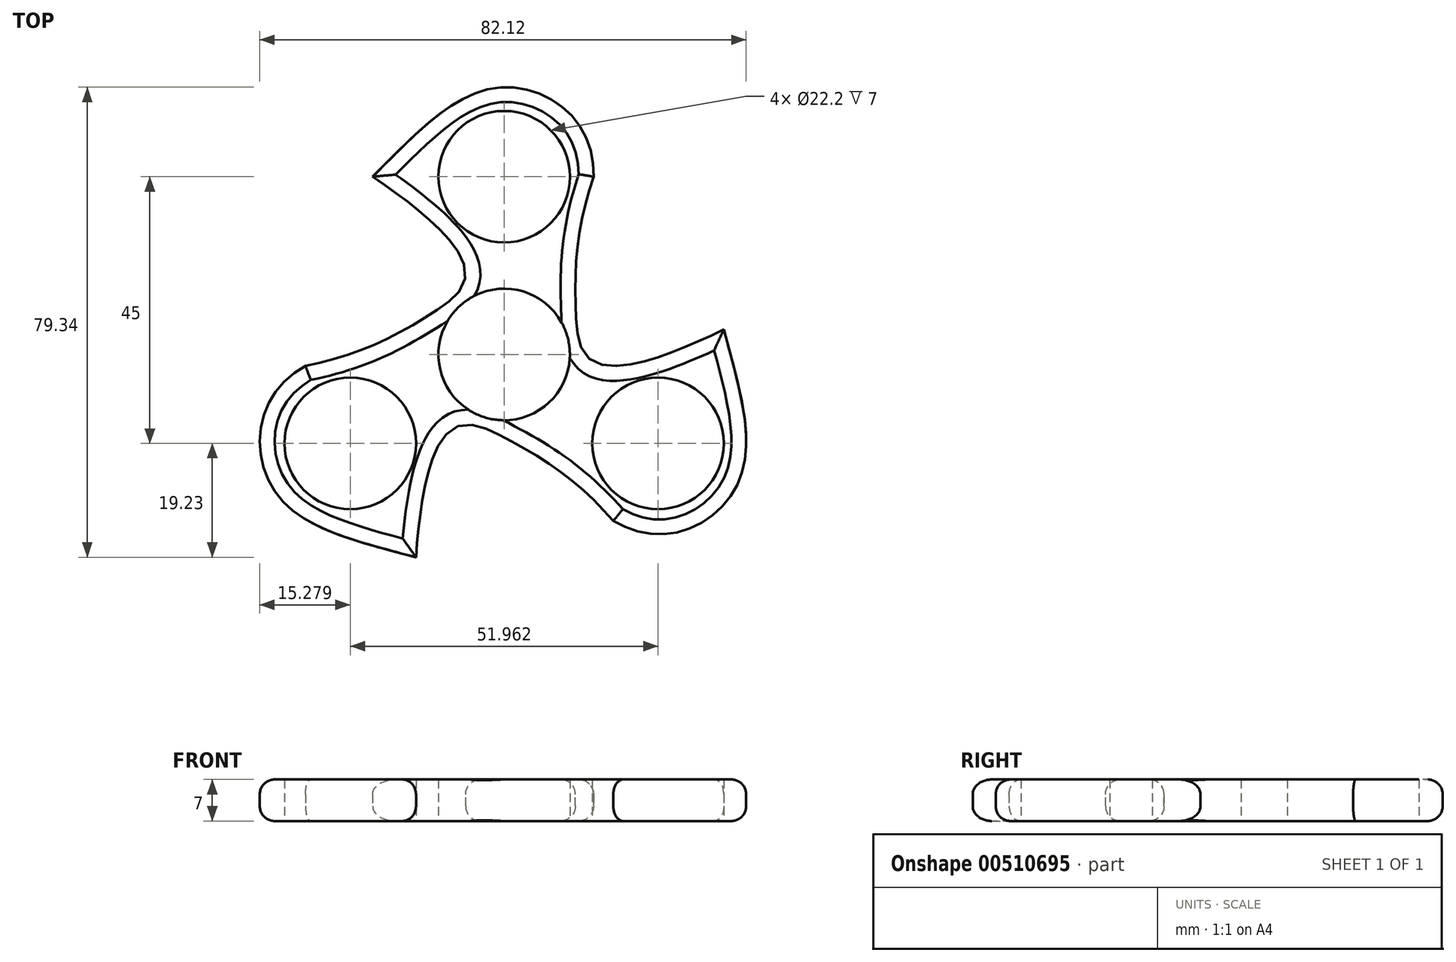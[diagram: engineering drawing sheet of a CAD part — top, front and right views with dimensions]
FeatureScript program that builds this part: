
annotation { "Feature Type Name" : "Feature", "Feature Type Description" : "" }
export const myFeature = defineFeature(function(context is Context, id is Id, definition is map)
    precondition{}
    {
        {
            var Q0;
            Q0=qCreatedBy(makeId("Top.planeOp"),FACE);
            var sketch = newSketch(context, id + "F0", { "sketchPlane" : qUnion([Q0])});
            skCircle(sketch, "E0", {"center": v(0, 0) * mm, "radius": 11.1 * mm});
            skCircle(sketch, "E1", {"center": v(0, 30) * mm, "radius": 11.1 * mm});
            skLineSegment(sketch, "E2", {"start": v(0, 0) * mm, "end": v(0, 30) * mm, "construction": true});
            skLineSegment(sketch, "E3", {"start": v(0, 30) * mm, "end": v(-22.2, 30) * mm, "construction": true});
            skLineSegment(sketch, "E4", {"start": v(0, 30) * mm, "end": v(15.1, 30) * mm, "construction": true});
            skLineSegment(sketch, "E5", {"start": v(0, 30) * mm, "end": v(0, 45.1) * mm, "construction": true});
            skLineSegment(sketch, "E6.1.0", {"start": v(-25.98, -15) * mm, "end": v(-33.53, -1.92) * mm, "construction": true});
            skLineSegment(sketch, "E6.1.1", {"start": v(-25.98, -15) * mm, "end": v(-39.06, -22.55) * mm, "construction": true});
            skLineSegment(sketch, "E6.1.2", {"start": v(-25.98, -15) * mm, "end": v(-14.88, -34.23) * mm, "construction": true});
            skCircle(sketch, "E6.1.3", {"center": v(-25.98, -15) * mm, "radius": 11.1 * mm});
            skLineSegment(sketch, "E6.1.4", {"start": v(0, 0) * mm, "end": v(-25.98, -15) * mm, "construction": true});
            skLineSegment(sketch, "E6.2.0", {"start": v(25.98, -15) * mm, "end": v(18.43, -28.08) * mm, "construction": true});
            skLineSegment(sketch, "E6.2.1", {"start": v(25.98, -15) * mm, "end": v(39.06, -22.55) * mm, "construction": true});
            skLineSegment(sketch, "E6.2.2", {"start": v(25.98, -15) * mm, "end": v(37.08, 4.23) * mm, "construction": true});
            skCircle(sketch, "E6.2.3", {"center": v(25.98, -15) * mm, "radius": 11.1 * mm});
            skLineSegment(sketch, "E6.2.4", {"start": v(0, 0) * mm, "end": v(25.98, -15) * mm, "construction": true});
            skLineSegment(sketch, "E7", {"start": v(0, 0) * mm, "end": v(-12.12, 7) * mm, "construction": true});
            skLineSegment(sketch, "E8.1.0", {"start": v(0, 0) * mm, "end": v(0, -14) * mm, "construction": true});
            skLineSegment(sketch, "E8.2.0", {"start": v(0, 0) * mm, "end": v(12.12, 7) * mm, "construction": true});
            skFitSpline(sketch, "E9", {"points": [v(-22.2, 30) * mm, v(0, 45.1) * mm, v(15.1, 30) * mm], "startDerivative": vector(44.63, 44.58) * mm, "endDerivative": vector(-1.2, -64.1) * mm});
            skFitSpline(sketch, "E10", {"points": [v(37.08, 4.23) * mm, v(39.06, -22.55) * mm, v(18.43, -28.08) * mm], "startDerivative": vector(16.3, -60.94) * mm, "endDerivative": vector(-54.91, 33.08) * mm});
            skFitSpline(sketch, "E11", {"points": [v(-14.88, -34.23) * mm, v(-39.06, -22.55) * mm, v(-33.53, -1.92) * mm], "startDerivative": vector(-60.93, 16.36) * mm, "endDerivative": vector(56.1, 31.02) * mm});
            skFitSpline(sketch, "E12", {"points": [v(15.1, 30) * mm, v(12.12, 7) * mm, v(37.08, 4.23) * mm], "startDerivative": vector(-19.55, -57.1) * mm, "endDerivative": vector(141.73, 68.98) * mm});
            skFitSpline(sketch, "E13", {"points": [v(18.43, -28.08) * mm, v(0, -14) * mm, v(-14.88, -34.23) * mm], "startDerivative": vector(-39.67, 45.48) * mm, "endDerivative": vector(-11.12, -157.23) * mm});
            skFitSpline(sketch, "E14", {"points": [v(-33.53, -1.92) * mm, v(-12.12, 7) * mm, v(-22.2, 30) * mm], "startDerivative": vector(59.23, 11.62) * mm, "endDerivative": vector(-130.6, 88.25) * mm});
            skLineSegment(sketch, "E15", {"start": v(18.43, -28.08) * mm, "end": v(27.06, -33.28) * mm});
            skLineSegment(sketch, "E16.1.0", {"start": v(15.1, 30) * mm, "end": v(15.29, 40.07) * mm});
            skLineSegment(sketch, "E16.2.0", {"start": v(-33.53, -1.92) * mm, "end": v(-42.35, -6.8) * mm});
            skSolve(sketch);
        }
        {
            var Q0;
            Q0=makeQuery(id+"F0.imprint","IMPRINT",FACE,{"disambiguationData":[TD([[makeQuery(id+"F0.imprint","IMPRINT",EDGE,{"derivedFrom":sQuery(id+"F0.wireOp",EDGE,"E0")}),-1.0]])]});
            extrude(context, id + "F1", {"entities" : qUnion([Q0]), "endBound" : BoundingType.SYMMETRIC, "depth" : 7 * mm});
        }
        {
            var Q0;
            Q0=makeQuery(id+"F1.opExtrude","CAP_EDGE",EDGE,{"disambiguationData":[OSD([sQuery(id+"F0.wireOp",EDGE,"E9")])],"isStart":false});
            var Q1;
            Q1=makeQuery(id+"F1.opExtrude","CAP_EDGE",EDGE,{"disambiguationData":[OSD([sQuery(id+"F0.wireOp",EDGE,"E12")])],"isStart":false});
            var Q2;
            Q2=makeQuery(id+"F1.opExtrude","CAP_EDGE",EDGE,{"disambiguationData":[OSD([sQuery(id+"F0.wireOp",EDGE,"E10")])],"isStart":false});
            var Q3;
            Q3=makeQuery(id+"F1.opExtrude","CAP_EDGE",EDGE,{"disambiguationData":[OSD([sQuery(id+"F0.wireOp",EDGE,"E13")])],"isStart":false});
            var Q4;
            Q4=makeQuery(id+"F1.opExtrude","CAP_EDGE",EDGE,{"disambiguationData":[OSD([sQuery(id+"F0.wireOp",EDGE,"E11")])],"isStart":false});
            var Q5;
            Q5=makeQuery(id+"F1.opExtrude","CAP_EDGE",EDGE,{"disambiguationData":[OSD([sQuery(id+"F0.wireOp",EDGE,"E14")])],"isStart":false});
            fillet(context, id + "F2", {"entities" : qUnion([Q0, Q1, Q2, Q3, Q4, Q5]), "radius" : 2.5 * mm, "tangentPropagation" : true, "allowEdgeOverflow" : false});
        }
        {
            var Q0;
            Q0=makeQuery(id+"F1.opExtrude","CAP_EDGE",EDGE,{"disambiguationData":[OSD([sQuery(id+"F0.wireOp",EDGE,"E10")])],"isStart":true});
            var Q1;
            Q1=makeQuery(id+"F1.opExtrude","CAP_EDGE",EDGE,{"disambiguationData":[OSD([sQuery(id+"F0.wireOp",EDGE,"E12")])],"isStart":true});
            var Q2;
            Q2=makeQuery(id+"F1.opExtrude","CAP_EDGE",EDGE,{"disambiguationData":[OSD([sQuery(id+"F0.wireOp",EDGE,"E13")])],"isStart":true});
            var Q3;
            Q3=makeQuery(id+"F1.opExtrude","CAP_EDGE",EDGE,{"disambiguationData":[OSD([sQuery(id+"F0.wireOp",EDGE,"E11")])],"isStart":true});
            var Q4;
            Q4=makeQuery(id+"F1.opExtrude","CAP_EDGE",EDGE,{"disambiguationData":[OSD([sQuery(id+"F0.wireOp",EDGE,"E14")])],"isStart":true});
            var Q5;
            Q5=makeQuery(id+"F1.opExtrude","CAP_EDGE",EDGE,{"disambiguationData":[OSD([sQuery(id+"F0.wireOp",EDGE,"E9")])],"isStart":true});
            fillet(context, id + "F3", {"entities" : qUnion([Q0, Q1, Q2, Q3, Q4, Q5]), "radius" : 2.5 * mm, "tangentPropagation" : true, "allowEdgeOverflow" : false});
        }
    });
